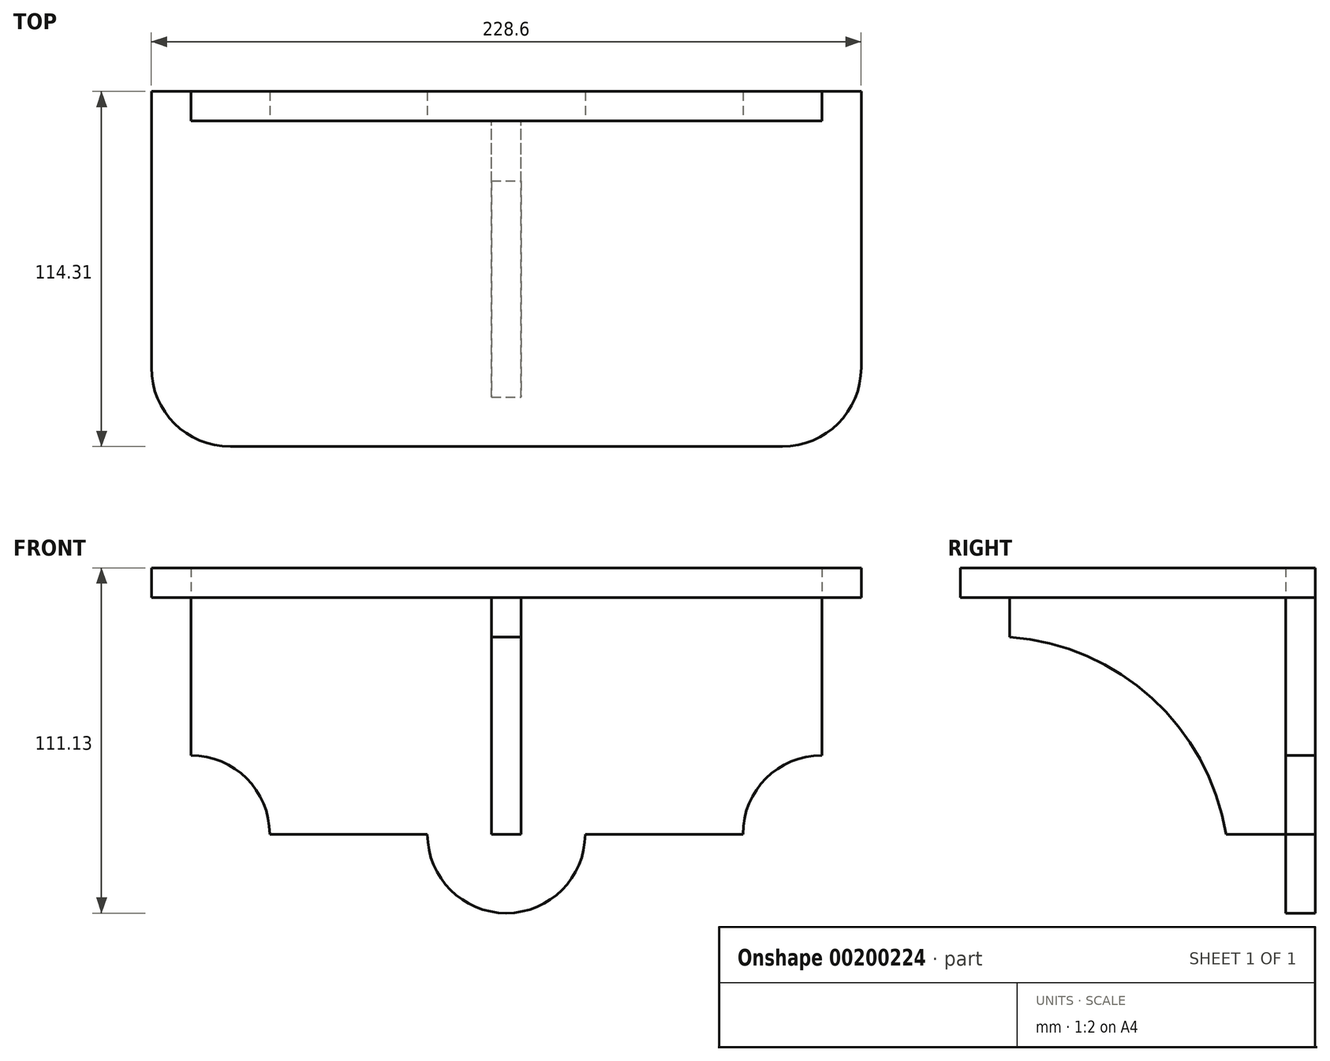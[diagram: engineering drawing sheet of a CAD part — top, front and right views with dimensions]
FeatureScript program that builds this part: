
annotation { "Feature Type Name" : "Feature", "Feature Type Description" : "" }
export const myFeature = defineFeature(function(context is Context, id is Id, definition is map)
    precondition{}
    {
        {
            var Q0;
            Q0=qCreatedBy(makeId("Front.planeOp"),FACE);
            var sketch = newSketch(context, id + "F0", { "sketchPlane" : qUnion([Q0])});
            skLineSegment(sketch, "E0.bottom", {"start": v(-86, 35.67) * mm, "end": v(117.2, 35.67) * mm});
            skLineSegment(sketch, "E0.top", {"start": v(-60.6, -40.53) * mm, "end": v(-9.8, -40.53) * mm});
            skLineSegment(sketch, "E0.left", {"start": v(-86, 35.67) * mm, "end": v(-86, -15.13) * mm});
            skLineSegment(sketch, "E0.right", {"start": v(117.2, 35.67) * mm, "end": v(117.2, -15.13) * mm});
            skArc(sketch, "E1", {"start": v(-60.6, -40.53) * mm, "mid": v(-68.04, -22.57) * mm, "end": v(-86, -15.13) * mm});
            skArc(sketch, "E2", {"start": v(117.2, -15.13) * mm, "mid": v(99.23, -22.57) * mm, "end": v(91.8, -40.53) * mm});
            skArc(sketch, "E3", {"start": v(-9.8, -40.53) * mm, "mid": v(15.6, -65.93) * mm, "end": v(41, -40.53) * mm});
            skLineSegment(sketch, "E4.trimOffspring", {"start": v(41, -40.53) * mm, "end": v(91.8, -40.53) * mm});
            skSolve(sketch);
        }
        {
            var Q0;
            Q0=makeQuery(id+"F0.imprint","IMPRINT",FACE,{"disambiguationData":[TD([[makeQuery(id+"F0.imprint","IMPRINT",EDGE,{"derivedFrom":sQuery(id+"F0.wireOp",EDGE,"E0.bottom")}),-1.0]])]});
            extrude(context, id + "F1", {"entities" : qUnion([Q0]), "oppositeDirection" : true, "depth" : 9.52 * mm});
        }
        {
            var Q0;
            Q0=makeQuery(id+"F1.opExtrude","SWEPT_FACE",FACE,{"disambiguationData":[OSD([sQuery(id+"F0.wireOp",EDGE,"E0.bottom")])]});
            var sketch = newSketch(context, id + "F2", { "sketchPlane" : qUnion([Q0])});
            skLineSegment(sketch, "E5.bottom", {"start": v(-98.7, 9.53) * mm, "end": v(129.9, 9.53) * mm});
            skLineSegment(sketch, "E5.top", {"start": v(-73.3, -104.78) * mm, "end": v(104.5, -104.78) * mm});
            skLineSegment(sketch, "E5.left", {"start": v(-98.7, 9.52) * mm, "end": v(-98.7, -79.38) * mm});
            skLineSegment(sketch, "E5.right", {"start": v(129.9, 9.52) * mm, "end": v(129.9, -79.38) * mm});
            skPoint(sketch, "E6.visualSharp", {"position": v(129.9, -104.78) * mm});
            skArc(sketch, "E6.filletArc", {"start": v(104.5, -104.78) * mm, "mid": v(122.46, -97.34) * mm, "end": v(129.9, -79.38) * mm});
            skPoint(sketch, "E7.visualSharp", {"position": v(-98.7, -104.78) * mm});
            skArc(sketch, "E7.filletArc", {"start": v(-98.7, -79.38) * mm, "mid": v(-91.27, -97.34) * mm, "end": v(-73.3, -104.78) * mm});
            skSolve(sketch);
        }
        {
            var Q0;
            Q0=makeQuery(id+"F2.imprint","IMPRINT",FACE,{"disambiguationData":[TD([[makeQuery(id+"F2.imprint","IMPRINT",EDGE,{"derivedFrom":sQuery(id+"F2.wireOp",EDGE,"E5.top")}),1.0]])]});
            extrude(context, id + "F3", {"entities" : qUnion([Q0]), "depth" : 9.52 * mm});
        }
        {
            var Q0;
            Q0=makeQuery(id+"F1.opExtrude","SWEPT_FACE",FACE,{"disambiguationData":[OSD([sQuery(id+"F0.wireOp",EDGE,"E0.bottom")])]});
            var sketch = newSketch(context, id + "F4", { "sketchPlane" : qUnion([Q0])});
            skLineSegment(sketch, "E8.bottom", {"start": v(117.2, 0) * mm, "end": v(-86, 0) * mm});
            skLineSegment(sketch, "E8.top", {"start": v(117.2, 9.53) * mm, "end": v(-86, 9.53) * mm});
            skLineSegment(sketch, "E8.left", {"start": v(117.2, 0) * mm, "end": v(117.2, 9.53) * mm});
            skLineSegment(sketch, "E8.right", {"start": v(-86, 0) * mm, "end": v(-86, 9.53) * mm});
            skSolve(sketch);
        }
        {
            var Q0;
            Q0=makeQuery(id+"F4.imprint","IMPRINT",FACE,{"disambiguationData":[TD([[makeQuery(id+"F4.imprint","IMPRINT",EDGE,{"derivedFrom":sQuery(id+"F4.wireOp",EDGE,"E8.bottom")}),1.0]])]});
            extrude(context, id + "F5", {"entities" : qUnion([Q0]), "depth" : 9.52 * mm});
        }
        {
            var Q0;
            Q0=makeQuery(id+"F1.opExtrude","CAP_FACE",FACE,{"disambiguationData":[OSD([sQuery(id+"F0.wireOp",EDGE,"E0.bottom"),sQuery(id+"F0.wireOp",EDGE,"E0.top"),sQuery(id+"F0.wireOp",EDGE,"E0.left"),sQuery(id+"F0.wireOp",EDGE,"E0.right"),sQuery(id+"F0.wireOp",EDGE,"E1"),sQuery(id+"F0.wireOp",EDGE,"E2"),sQuery(id+"F0.wireOp",EDGE,"E3"),sQuery(id+"F0.wireOp",EDGE,"E4.trimOffspring")])],"isStart":true});
            var sketch = newSketch(context, id + "F6", { "sketchPlane" : qUnion([Q0])});
            skLineSegment(sketch, "E9.bottom", {"start": v(10.83, 35.67) * mm, "end": v(20.36, 35.67) * mm});
            skLineSegment(sketch, "E9.top", {"start": v(10.83, -40.53) * mm, "end": v(20.36, -40.53) * mm});
            skLineSegment(sketch, "E9.left", {"start": v(10.83, 35.67) * mm, "end": v(10.83, -40.53) * mm});
            skLineSegment(sketch, "E9.right", {"start": v(20.36, 35.67) * mm, "end": v(20.36, -40.53) * mm});
            skPoint(sketch, "E10.endSnap0", {"position": v(15.6, -40.53) * mm});
            skSolve(sketch);
        }
        {
            var Q0;
            Q0=makeQuery(id+"F6.imprint","IMPRINT",FACE,{"disambiguationData":[TD([[makeQuery(id+"F6.imprint","IMPRINT",EDGE,{"derivedFrom":sQuery(id+"F6.wireOp",EDGE,"E9.bottom")}),-1.0]])]});
            extrude(context, id + "F7", {"entities" : qUnion([Q0]), "depth" : 88.9 * mm});
        }
        {
            var Q0;
            Q0=makeQuery(id+"F7.opExtrude","SWEPT_FACE",FACE,{"disambiguationData":[OSD([sQuery(id+"F6.wireOp",EDGE,"E9.right")])]});
            var sketch = newSketch(context, id + "F8", { "sketchPlane" : qUnion([Q0])});
            skCircle(sketch, "E11", {"center": v(-94.42, -53.06) * mm, "radius": 76.2 * mm});
            skSolve(sketch);
        }
        {
            var Q0;
            {var subQ0=sQuery(id+"F8.wireOp",EDGE,"E11");var subQ1=sQuery(id+"F6.wireOp",EDGE,"E9.right");var subQ4=makeQuery(id+"F7.opExtrude","CAP_EDGE",EDGE,{"disambiguationData":[OSD([subQ1])],"isStart":false});var subQ5=makeQuery(id+"F8.imprint","INTERSECT",VERTEX,{"derivedFrom":[subQ4,subQ0]});Q0=makeQuery(id+"F8.imprint","IMPRINT",FACE,{"disambiguationData":[TD([[makeQuery(id+"F8.imprint","IMPRINT",EDGE,{"disambiguationData":[TD([[subQ5,-1.0]])],"derivedFrom":subQ0}),1.0]])]});}
            var Q1;
            {var subQ0=sQuery(id+"F8.wireOp",EDGE,"E11");var subQ1=sQuery(id+"F6.wireOp",EDGE,"E9.right");var subQ4=makeQuery(id+"F7.opExtrude","CAP_EDGE",EDGE,{"disambiguationData":[OSD([subQ1])],"isStart":false});var subQ5=makeQuery(id+"F8.imprint","INTERSECT",VERTEX,{"derivedFrom":[subQ4,subQ0]});Q1=makeQuery(id+"F8.imprint","IMPRINT",FACE,{"disambiguationData":[TD([[makeQuery(id+"F8.imprint","IMPRINT",EDGE,{"disambiguationData":[TD([[subQ5,1.0]])],"derivedFrom":subQ0}),1.0]])]});}
            extrude(context, id + "F9", {"entities" : qUnion([Q0, Q1]), "operationType" : NewBodyOperationType.REMOVE, "oppositeDirection" : true, "depth" : 19.3 * mm});
        }
    });
